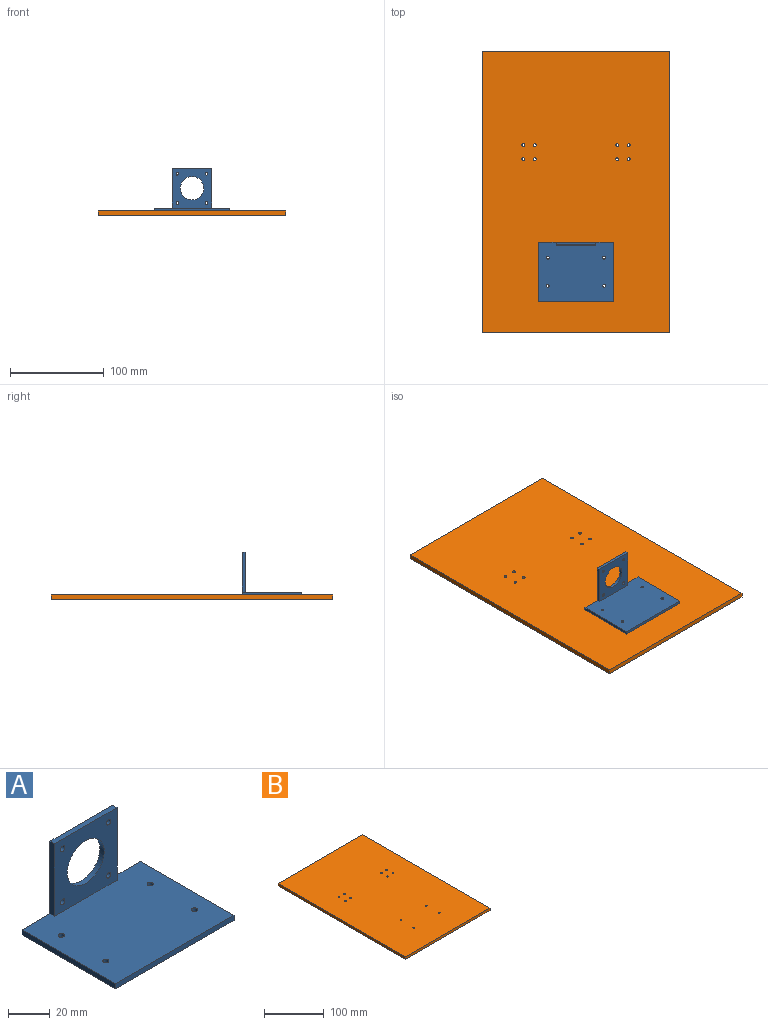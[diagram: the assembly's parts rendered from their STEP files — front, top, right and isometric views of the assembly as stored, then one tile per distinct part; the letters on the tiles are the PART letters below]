
ASSEMBLY  parts=2 mates=1
PART A: 19 faces, bbox 80x63x45.3 mm
  f0: plane 80x63mm, normal (0,0,1), area 4884.8mm2, adj f2,f3,f4,f5,f6,f7,f8,f9
  f1: plane 80x63mm, normal (0,0,-1), area 5011.7mm2, adj f2,f3,f4,f5,f6,f7,f8,f9
  f2: plane 63x3mm, normal (-1,0,0), area 189mm2, adj f0,f1,f3,f5
  f3: plane 80x3mm, normal (0,-1,0), area 240mm2, adj f0,f1,f2,f4
  f4: plane 63x3mm, normal (1,0,0), area 189mm2, adj f0,f1,f3,f5
  f5: plane 80x45.3mm, normal (0,1,0), area 1510.1mm2, adj f0,f1,f2,f4,f10,f11,f12,f14
  f6: cylinder r=1.5mm len=3mm, axis (0,0,-1), area 28.3mm2, adj f0,f1
  f7: cylinder r=1.5mm len=3mm, axis (0,0,-1), area 28.3mm2, adj f0,f1
  f8: cylinder r=1.5mm len=3mm, axis (0,0,-1), area 28.3mm2, adj f0,f1
  f9: cylinder r=1.5mm len=3mm, axis (0,0,-1), area 28.3mm2, adj f0,f1
  f10: plane 42.3x3mm, normal (1,0,0), area 126.9mm2, adj f0,f5,f11,f13
  f11: plane 42.3x3mm, normal (0,0,1), area 126.9mm2, adj f5,f10,f12,f13
  f12: plane 42.3x3mm, normal (-1,0,0), area 126.9mm2, adj f0,f5,f11,f13
  f13: plane 42.3x42.3mm, normal (0,-1,0), area 1270.1mm2, adj f0,f10,f11,f12,f14,f15,f16,f17
  f14: cylinder r=1.5mm len=3mm, axis (0,1,0), area 28.3mm2, adj f5,f13
  f15: cylinder r=1.5mm len=3mm, axis (0,1,0), area 28.3mm2, adj f5,f13
  f16: cylinder r=1.5mm len=3mm, axis (0,1,0), area 28.3mm2, adj f5,f13
  f17: cylinder r=1.5mm len=3mm, axis (0,1,0), area 28.3mm2, adj f5,f13
  f18: cylinder r=12.5mm len=25mm, axis (0,1,0), area 235.6mm2, adj f5,f13
PART B: 18 faces, bbox 200x300x5 mm
  f0: plane 300x200mm, normal (0,0,1), area 59915.2mm2, adj f2,f3,f4,f5,f6,f7,f8,f9
  f1: plane 300x200mm, normal (0,0,-1), area 59915.2mm2, adj f2,f3,f4,f5,f6,f7,f8,f9
  f2: plane 300x5mm, normal (-1,0,0), area 1500mm2, adj f0,f1,f3,f5
  f3: plane 200x5mm, normal (0,-1,0), area 1000mm2, adj f0,f1,f2,f4
  f4: plane 300x5mm, normal (1,0,0), area 1500mm2, adj f0,f1,f3,f5
  f5: plane 200x5mm, normal (0,1,0), area 1000mm2, adj f0,f1,f2,f4
  f6: cylinder r=1.5mm len=5mm, axis (0,0,-1), area 47.1mm2, adj f0,f1
  f7: cylinder r=1.5mm len=5mm, axis (0,0,-1), area 47.1mm2, adj f0,f1
  f8: cylinder r=1.5mm len=5mm, axis (0,0,-1), area 47.1mm2, adj f0,f1
  f9: cylinder r=1.5mm len=5mm, axis (0,0,-1), area 47.1mm2, adj f0,f1
  f10: cylinder r=1.5mm len=5mm, axis (0,0,-1), area 47.1mm2, adj f0,f1
  f11: cylinder r=1.5mm len=5mm, axis (0,0,-1), area 47.1mm2, adj f0,f1
  f12: cylinder r=1.5mm len=5mm, axis (0,0,-1), area 47.1mm2, adj f0,f1
  f13: cylinder r=1.5mm len=5mm, axis (0,0,-1), area 47.1mm2, adj f0,f1
  f14: cylinder r=1.5mm len=5mm, axis (0,0,-1), area 47.1mm2, adj f0,f1
  f15: cylinder r=1.5mm len=5mm, axis (0,0,-1), area 47.1mm2, adj f0,f1
  f16: cylinder r=1.5mm len=5mm, axis (0,0,-1), area 47.1mm2, adj f0,f1
  f17: cylinder r=1.5mm len=5mm, axis (0,0,-1), area 47.1mm2, adj f0,f1
PLACE A t=(-46.09,-122.49,-1.21)mm
PLACE B t=(-6.09,-5.99,-6.21)mm fixed
MATE fastened B.f15 <-> A.f7  axis (0,0,1) through (-36.09,-105.99,-1.21)mm
